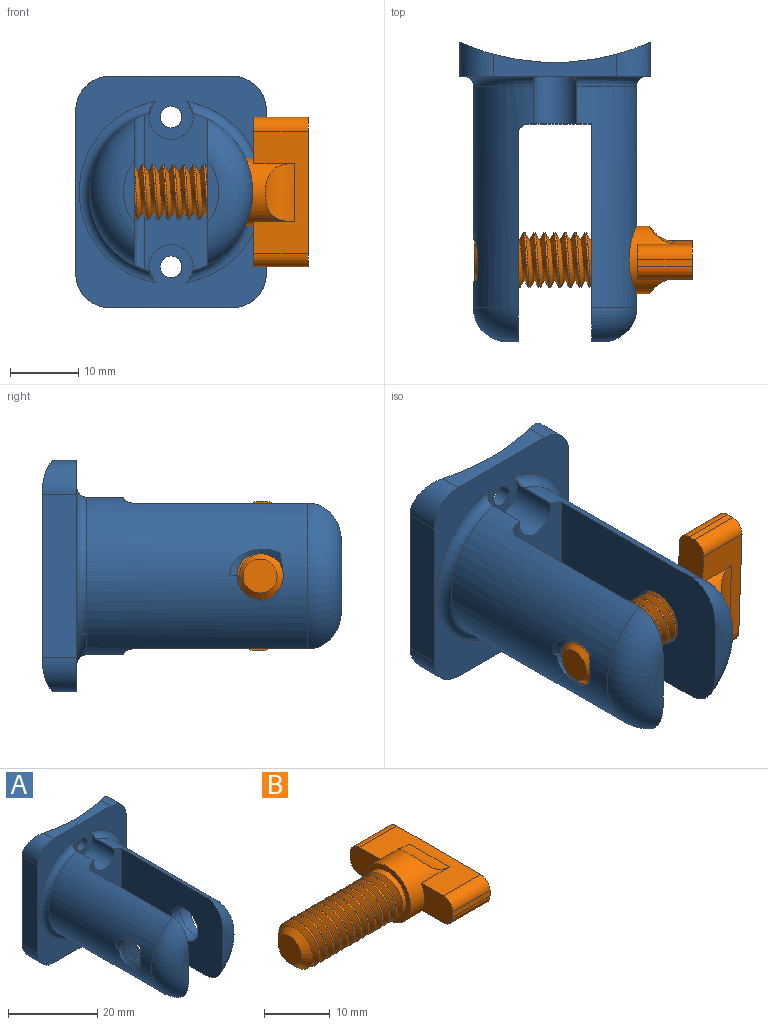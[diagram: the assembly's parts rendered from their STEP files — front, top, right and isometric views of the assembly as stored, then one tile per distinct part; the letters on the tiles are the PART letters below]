
ASSEMBLY  parts=2 mates=1
PART A: 37 faces, bbox 31.5x44x34 mm
  f0: plane 18x3.21mm, normal (0,0,-1), area 43.2mm2, adj f11,f19,f20,f31
  f1: plane 25.19x0.04mm, normal (0,1,0), area 0.9mm2, adj f15,f16,f19,f31
  f2: cylinder r=12mm len=32.5mm, axis (0,1,0), area 843.6mm2, adj f3,f4,f7,f8,f22,f24,f28,f29
  f3: cylinder r=3.4mm len=3.51mm, axis (1,0,0), area 0mm2, adj f2,f29
  f4: cylinder r=3.4mm len=6.8mm, axis (1,0,0), area 15.8mm2, adj f2,f27,f28,f29,f30
  f5: cylinder r=12mm len=32.5mm, axis (0,1,0), area 803.4mm2, adj f7,f8,f23,f24,f25,f33,f36
  f6: cylinder r=4.25mm len=8.5mm, axis (-1,0,0), area 80.1mm2, adj f23,f26
  f7: cylinder r=3.25mm len=7mm, axis (0,1,0), area 82.4mm2, adj f2,f5,f20,f24,f35,f36
  f8: cylinder r=3.25mm len=7mm, axis (0,1,0), area 82.4mm2, adj f2,f5,f20,f24,f35,f36
  f9: plane 8.91x1.6mm, normal (0,-1,0), area 9.7mm2, adj f22,f32
  f10: plane 8.91x1.6mm, normal (0,-1,0), area 9.7mm2, adj f23,f33
  f11: cylinder r=5mm len=5mm, axis (0,1,0), area 32.8mm2, adj f0,f12,f20,f21,f31
  f12: plane 24x5mm, normal (1,0,0), area 120mm2, adj f11,f13,f20,f21
  f13: cylinder r=5mm len=5mm, axis (0,1,0), area 32.8mm2, adj f12,f14,f20,f21,f31
  f14: plane 18x3.21mm, normal (0,0,1), area 43.2mm2, adj f13,f15,f20,f31
  f15: cylinder r=5mm len=5mm, axis (0,1,0), area 32.8mm2, adj f1,f14,f16,f20,f31
  f16: plane 24x5mm, normal (-1,0,0), area 120mm2, adj f1,f15,f19,f20
  f17: cylinder r=1.6mm len=3.2mm, axis (0,1,0), area 20.1mm2, adj f20,f31
  f18: cylinder r=1.6mm len=3.2mm, axis (0,1,0), area 20.1mm2, adj f20,f31
  f19: cylinder r=5mm len=5mm, axis (0,1,0), area 32.8mm2, adj f0,f1,f16,f20,f31
  f20: plane 34x28mm, normal (0,-1,0), area 403.5mm2, adj f0,f7,f8,f11,f12,f13,f14,f15
  f21: plane 25.19x0.04mm, normal (0,1,0), area 0.9mm2, adj f11,f12,f13,f31
  f22: plane 30.5x21.43mm, normal (1,0,0), area 565.8mm2, adj f2,f9,f27,f32,f34
  f23: plane 32x21.43mm, normal (-1,0,0), area 616.7mm2, adj f5,f6,f10,f24,f33
  f24: plane 23.13x9.3mm, normal (0,-1,0), area 172.8mm2, adj f2,f5,f7,f8,f23,f34
  f25: cylinder r=5.1mm len=10.2mm, axis (-1,0,0), area 97.4mm2, adj f5,f26
  f26: plane 10.2x10.2mm, normal (1,0,0), area 25mm2, adj f6,f25
  f27: cone r=4.9mm half-angle=45deg, axis (1,0,0), area 40.1mm2, adj f4,f22,f29,f30
  f28: plane 1.02x0.61mm, normal (0,0,1), area 0.3mm2, adj f2,f4,f30
  f29: bspline ~10.32x8.93mm, area 110.4mm2, adj f2,f3,f4,f27,f30
  f30: bspline ~10.32x8.93mm, area 104.6mm2, adj f2,f4,f27,f28,f29
  f31: cylinder r=34mm len=34mm, axis (0,0,-1), area 939.9mm2, adj f0,f1,f11,f13,f14,f15,f17,f18
  f32: torus R=7mm, axis (0,-1,0), area 161.3mm2, adj f2,f9,f22
  f33: torus R=7mm, axis (0,-1,0), area 161.3mm2, adj f5,f10,f23
  f34: cylinder r=1.5mm len=22.7mm, axis (0,0,1), area 52mm2, adj f2,f22,f24
  f35: torus R=13.5mm, axis (0,-1,0), area 79.9mm2, adj f2,f7,f8,f20
  f36: torus R=13.5mm, axis (0,-1,0), area 79.9mm2, adj f5,f7,f8,f20
PART B: 23 faces, bbox 32.5x22x9.9 mm
  f0: cylinder r=4.95mm len=9.9mm, axis (-1,0,0), area 145.4mm2, adj f3,f10,f11,f12,f20,f21,f22
  f1: cylinder r=4mm len=19.5mm, axis (1,0,0), area 77.4mm2, adj f3,f4,f7,f8,f9
  f2: plane 5x5mm, normal (-1,0,0), area 19.6mm2, adj f5
  f3: plane 9.92x9.92mm, normal (-1,0,0), area 26.5mm2, adj f0,f1,f6,f8,f9
  f4: cone r=4mm half-angle=45deg, axis (1,0,0), area 2.5mm2, adj f1,f5,f7,f8
  f5: cone r=4mm half-angle=45deg, axis (1,0,0), area 26.5mm2, adj f2,f4,f7,f8
  f6: cylinder r=4.14mm len=2.37mm, axis (-1,0,0), area 0.2mm2, adj f3,f8,f9
  f7: bspline ~20.95x9.56mm, area 344.7mm2, adj f1,f4,f5,f8,f9
  f8: bspline ~20.95x9.56mm, area 357.1mm2, adj f1,f3,f4,f5,f6,f7,f9
  f9: plane 1.32x1.21mm, normal (0,0,-1), area 0.7mm2, adj f1,f3,f6,f7,f8
  f10: plane 6.73x5mm, normal (-1,0,0), area 29.6mm2, adj f0,f11,f12,f13,f14,f15
  f11: plane 18x8mm, normal (0,0,-1), area 92.7mm2, adj f0,f10,f13,f18,f19,f20,f21
  f12: plane 18x8mm, normal (0,0,1), area 92.7mm2, adj f0,f10,f15,f16,f19,f20,f22
  f13: cylinder r=2mm len=8mm, axis (-1,0,0), area 25.1mm2, adj f10,f11,f14,f19
  f14: plane 8x1mm, normal (0,1,0), area 8mm2, adj f10,f13,f15,f19
  f15: cylinder r=2mm len=8mm, axis (-1,0,0), area 25.1mm2, adj f10,f12,f14,f19
  f16: cylinder r=2mm len=8mm, axis (-1,0,0), area 25.1mm2, adj f12,f17,f19,f20
  f17: plane 8x1mm, normal (0,-1,0), area 8mm2, adj f16,f18,f19,f20
  f18: cylinder r=2mm len=8mm, axis (-1,0,0), area 25.1mm2, adj f11,f17,f19,f20
  f19: plane 22x5mm, normal (1,0,0), area 106.6mm2, adj f11,f12,f13,f14,f15,f16,f17,f18
  f20: plane 6.73x5mm, normal (-1,0,0), area 29.6mm2, adj f0,f11,f12,f16,f17,f18
  f21: cylinder r=5mm len=8.54mm, axis (0,-1,0), area 35.7mm2, adj f0,f11
  f22: cylinder r=5mm len=8.54mm, axis (0,1,0), area 35.7mm2, adj f0,f12
PLACE A t=(-4.8,31.82,-17.77)mm fixed
PLACE B rot(axis=(1,0,0),92.1deg) t=(-22.57,-0.18,-0.85)mm
MATE cylindrical A.f6 <-> B.f0  axis (1,0,0) through (-23.32,-0.18,-0.85)mm
